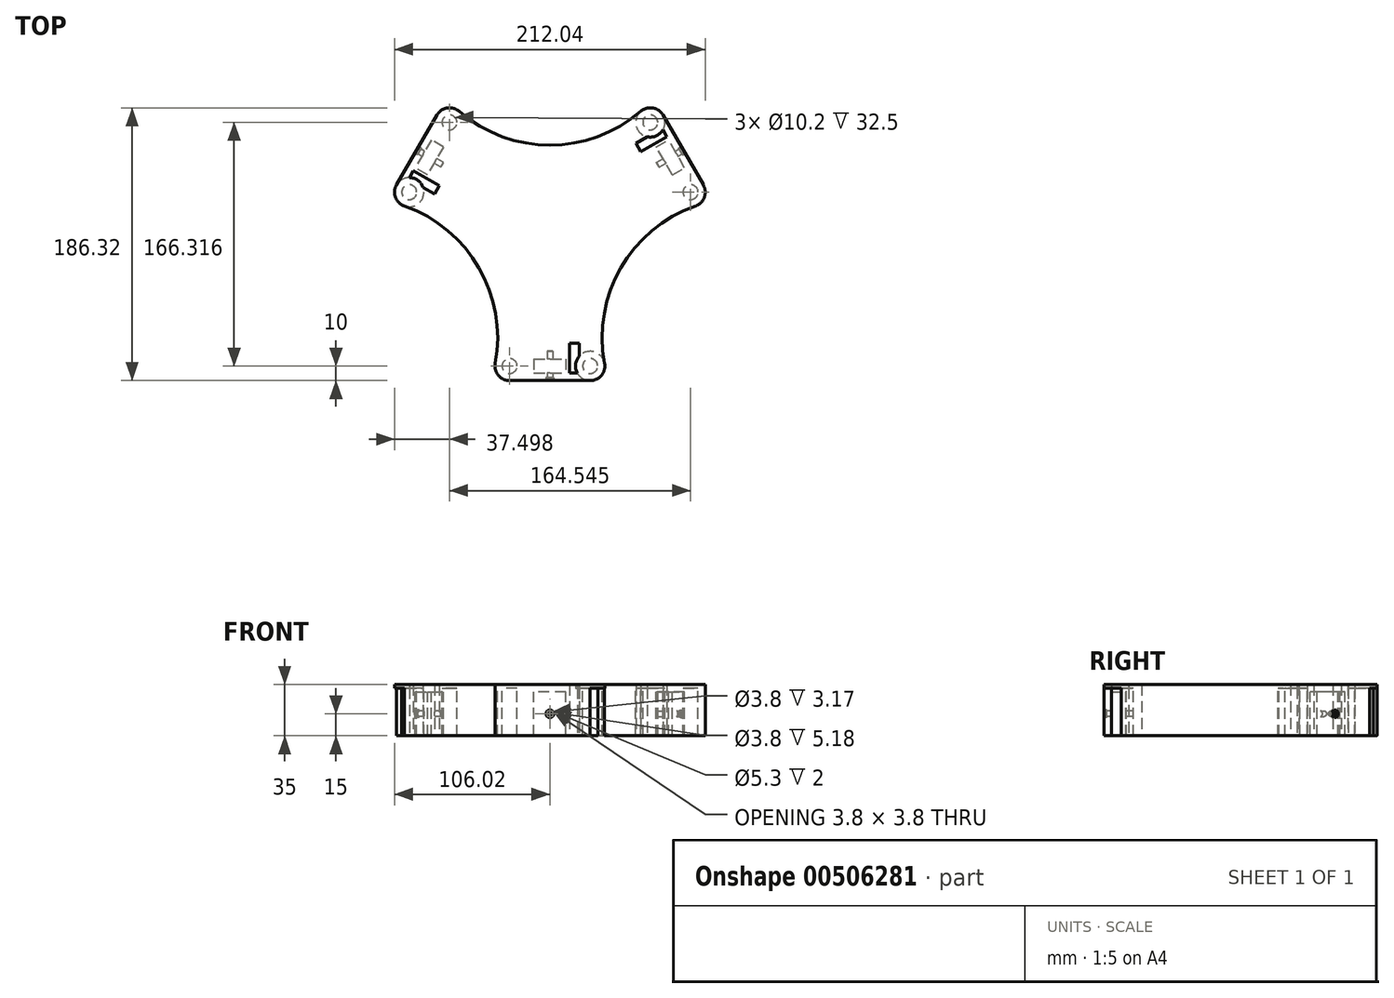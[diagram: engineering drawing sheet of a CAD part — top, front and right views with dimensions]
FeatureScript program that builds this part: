
annotation { "Feature Type Name" : "Feature", "Feature Type Description" : "" }
export const myFeature = defineFeature(function(context is Context, id is Id, definition is map)
    precondition{}
    {
        {
            var Q0;
            Q0=qCreatedBy(makeId("Top.planeOp"),FACE);
            var sketch = newSketch(context, id + "F0", { "sketchPlane" : qUnion([Q0])});
            skCircle(sketch, "E0", {"center": v(0, 0) * mm, "radius": 57.15 * mm, "construction": true});
            skLineSegment(sketch, "E1.bottom", {"start": v(110, -110) * mm, "end": v(-110, -110) * mm, "construction": true});
            skLineSegment(sketch, "E1.top", {"start": v(110, 110) * mm, "end": v(-110, 110) * mm, "construction": true});
            skLineSegment(sketch, "E1.left", {"start": v(110, -110) * mm, "end": v(110, 110) * mm, "construction": true});
            skLineSegment(sketch, "E1.right", {"start": v(-110, -110) * mm, "end": v(-110, 110) * mm, "construction": true});
            skLineSegment(sketch, "E2", {"start": v(0, 0) * mm, "end": v(0, -95) * mm});
            skLineSegment(sketch, "E3", {"start": v(0, 0) * mm, "end": v(-69.71, -40.25) * mm});
            skLineSegment(sketch, "E4", {"start": v(0, 0) * mm, "end": v(-77.38, 44.67) * mm});
            skLineSegment(sketch, "E5.MirrorCS", {"start": v(0, 0) * mm, "end": v(69.71, -40.25) * mm});
            skLineSegment(sketch, "E6.MirrorCS", {"start": v(0, 0) * mm, "end": v(77.38, 44.67) * mm});
            skCircle(sketch, "E7", {"center": v(-27.5, -95) * mm, "radius": 5.1 * mm});
            skCircle(sketch, "E8", {"center": v(-27.5, -95) * mm, "radius": 10 * mm});
            skCircle(sketch, "E9.MirrorC", {"center": v(27.5, -95) * mm, "radius": 5.1 * mm});
            skCircle(sketch, "E10.MirrorC", {"center": v(27.5, -95) * mm, "radius": 10 * mm});
            skLineSegment(sketch, "E11", {"start": v(-27.5, -105) * mm, "end": v(27.5, -105) * mm});
            skCircle(sketch, "E12.1.0", {"center": v(96.02, 23.68) * mm, "radius": 5.1 * mm});
            skCircle(sketch, "E12.1.1", {"center": v(96.02, 23.68) * mm, "radius": 10 * mm});
            skLineSegment(sketch, "E12.1.2", {"start": v(104.68, 28.68) * mm, "end": v(77.18, 76.32) * mm});
            skCircle(sketch, "E12.1.3", {"center": v(68.52, 71.32) * mm, "radius": 10 * mm});
            skCircle(sketch, "E12.1.4", {"center": v(68.52, 71.32) * mm, "radius": 5.1 * mm});
            skCircle(sketch, "E12.2.0", {"center": v(-68.52, 71.32) * mm, "radius": 5.1 * mm});
            skCircle(sketch, "E12.2.1", {"center": v(-68.52, 71.32) * mm, "radius": 10 * mm});
            skLineSegment(sketch, "E12.2.2", {"start": v(-77.18, 76.32) * mm, "end": v(-104.68, 28.68) * mm});
            skCircle(sketch, "E12.2.3", {"center": v(-96.02, 23.68) * mm, "radius": 10 * mm});
            skCircle(sketch, "E12.2.4", {"center": v(-96.02, 23.68) * mm, "radius": 5.1 * mm});
            skArc(sketch, "E13", {"start": v(99.32, 14.24) * mm, "mid": v(48.39, -27.94) * mm, "end": v(37.32, -93.14) * mm});
            skArc(sketch, "E14.1.0", {"start": v(-62, 78.9) * mm, "mid": v(0, 55.87) * mm, "end": v(62, 78.9) * mm});
            skArc(sketch, "E14.2.0", {"start": v(-37.32, -93.14) * mm, "mid": v(-48.39, -27.94) * mm, "end": v(-99.32, 14.24) * mm});
            skSolve(sketch);
        }
        {
            var Q0;
            {var subQ0=sQuery(id+"F0.wireOp",EDGE,"E11");Q0=makeQuery(id+"F0.imprint","IMPRINT",FACE,{"disambiguationData":[TD([[makeQuery(id+"F0.imprint","IMPRINT",EDGE,{"derivedFrom":subQ0}),1.0]])]});}
            var Q1;
            Q1=makeQuery(id+"F0.imprint","IMPRINT",FACE,{"disambiguationData":[TD([[makeQuery(id+"F0.imprint","IMPRINT",EDGE,{"derivedFrom":sQuery(id+"F0.wireOp",EDGE,"E9.MirrorC")}),1.0]])]});
            var Q2;
            Q2=makeQuery(id+"F0.imprint","IMPRINT",FACE,{"disambiguationData":[TD([[makeQuery(id+"F0.imprint","IMPRINT",EDGE,{"derivedFrom":sQuery(id+"F0.wireOp",EDGE,"E7")}),-1.0]])]});
            extrude(context, id + "F1", {"entities" : qUnion([Q0, Q1, Q2]), "oppositeDirection" : true, "depth" : 35 * mm});
        }
        {
            var Q0;
            {var subQ0=sQuery(id+"F0.wireOp",EDGE,"E11");Q0=makeQuery(id+"F0.imprint","IMPRINT",FACE,{"disambiguationData":[TD([[makeQuery(id+"F0.imprint","IMPRINT",EDGE,{"derivedFrom":subQ0}),1.0]])]});}
            var sketch = newSketch(context, id + "F2", { "sketchPlane" : qUnion([Q0])});
            skLineSegment(sketch, "E15.0", {"start": v(-27.5, -105) * mm, "end": v(27.5, -105) * mm});
            skLineSegment(sketch, "E16.bottom", {"start": v(11, -99.83) * mm, "end": v(-11, -99.83) * mm});
            skLineSegment(sketch, "E16.top", {"start": v(11, -90.18) * mm, "end": v(-11, -90.18) * mm});
            skLineSegment(sketch, "E16.left", {"start": v(11, -99.83) * mm, "end": v(11, -90.18) * mm});
            skLineSegment(sketch, "E16.right", {"start": v(-11, -99.83) * mm, "end": v(-11, -90.18) * mm});
            skPoint(sketch, "E16.middle", {"position": v(0, -95) * mm});
            skPoint(sketch, "E16.middle.positionSnap0", {"position": v(0, -105) * mm});
            skPoint(sketch, "E16.centerSnap0", {"position": v(0, -105) * mm});
            skSolve(sketch);
        }
        {
            var Q0;
            Q0=makeQuery(id+"F2.imprint","IMPRINT",FACE,{"disambiguationData":[TD([[makeQuery(id+"F2.imprint","IMPRINT",EDGE,{"derivedFrom":sQuery(id+"F2.wireOp",EDGE,"E16.bottom")}),-1.0]])]});
            var Q1;
            Q1=makeQuery(id+"F1.opExtrude","CAP_FACE",FACE,{"disambiguationData":[OSD([sQuery(id+"F0.wireOp",EDGE,"E3"),sQuery(id+"F0.wireOp",EDGE,"E5.MirrorCS"),sQuery(id+"F0.wireOp",EDGE,"E7"),sQuery(id+"F0.wireOp",EDGE,"E8"),sQuery(id+"F0.wireOp",EDGE,"E9.MirrorC"),sQuery(id+"F0.wireOp",EDGE,"E10.MirrorC"),sQuery(id+"F0.wireOp",EDGE,"E11"),sQuery(id+"F0.wireOp",EDGE,"E13"),sQuery(id+"F0.wireOp",EDGE,"E14.2.0")])],"isStart":false});
            extrude(context, id + "F3", {"entities" : qUnion([Q0]), "operationType" : NewBodyOperationType.REMOVE, "endBound" : BoundingType.UP_TO_SURFACE, "oppositeDirection" : true, "endBoundEntityFace" : qUnion([Q1]), "depth" : 25 * mm});
        }
        {
            var Q0;
            Q0=makeQuery(id+"F2.imprint","IMPRINT",FACE,{"disambiguationData":[TD([[makeQuery(id+"F2.imprint","IMPRINT",EDGE,{"derivedFrom":sQuery(id+"F2.wireOp",EDGE,"E16.bottom")}),-1.0]])]});
            extrude(context, id + "F4", {"entities" : qUnion([Q0]), "operationType" : NewBodyOperationType.ADD, "oppositeDirection" : true, "depth" : 5 * mm});
        }
        {
            var Q0;
            Q0=makeQuery(id+"F0.imprint","IMPRINT",FACE,{"disambiguationData":[TD([[makeQuery(id+"F0.imprint","IMPRINT",EDGE,{"derivedFrom":sQuery(id+"F0.wireOp",EDGE,"E7")}),1.0]])]});
            var Q1;
            Q1=makeQuery(id+"F0.imprint","IMPRINT",FACE,{"disambiguationData":[TD([[makeQuery(id+"F0.imprint","IMPRINT",EDGE,{"derivedFrom":sQuery(id+"F0.wireOp",EDGE,"E9.MirrorC")}),-1.0]])]});
            var Q2;
            Q2=sQuery(id+"F0.wireOp",EDGE,"E7");
            var Q3;
            Q3=sQuery(id+"F0.wireOp",EDGE,"E9.MirrorC");
            extrude(context, id + "F5", {"entities" : qUnion([Q0, Q1]), "operationType" : NewBodyOperationType.ADD, "surfaceEntities" : qUnion([Q2, Q3]), "oppositeDirection" : true, "depth" : 2.5 * mm});
        }
        {
            var Q0;
            Q0=makeQuery(id+"F1.opExtrude","SWEPT_FACE",FACE,{"disambiguationData":[OSD([sQuery(id+"F0.wireOp",EDGE,"E11")])]});
            var sketch = newSketch(context, id + "F6", { "sketchPlane" : qUnion([Q0])});
            skLineSegment(sketch, "E17.0", {"start": v(-27.5, -35) * mm, "end": v(27.5, -35) * mm});
            skLineSegment(sketch, "E18.0", {"start": v(-27.5, 0) * mm, "end": v(27.5, 0) * mm});
            skLineSegment(sketch, "E19", {"start": v(0, 0) * mm, "end": v(0, -35) * mm, "construction": true});
            skPoint(sketch, "E20", {"position": v(0, -17.5) * mm});
            skCircle(sketch, "E21", {"center": v(0, -20) * mm, "radius": 4.15 * mm});
            skCircle(sketch, "E22", {"center": v(0, -20) * mm, "radius": 2.65 * mm});
            skCircle(sketch, "E23", {"center": v(0, -20) * mm, "radius": 1.9 * mm});
            skSolve(sketch);
        }
        {
            var Q0;
            Q0=makeQuery(id+"F6.imprint","IMPRINT",FACE,{"disambiguationData":[TD([[makeQuery(id+"F6.imprint","IMPRINT",EDGE,{"derivedFrom":sQuery(id+"F6.wireOp",EDGE,"E23")}),1.0]])]});
            extrude(context, id + "F7", {"entities" : qUnion([Q0]), "operationType" : NewBodyOperationType.REMOVE, "oppositeDirection" : true, "depth" : 20 * mm});
        }
        {
            var Q0;
            Q0=makeQuery(id+"F6.imprint","IMPRINT",FACE,{"disambiguationData":[TD([[makeQuery(id+"F6.imprint","IMPRINT",EDGE,{"derivedFrom":sQuery(id+"F6.wireOp",EDGE,"E22")}),1.0]])]});
            extrude(context, id + "F8", {"entities" : qUnion([Q0]), "operationType" : NewBodyOperationType.REMOVE, "oppositeDirection" : true, "depth" : 2 * mm});
        }
        {
            var Q0;
            Q0=makeQuery(id+"F1.opExtrude","CAP_FACE",FACE,{"disambiguationData":[OSD([sQuery(id+"F0.wireOp",EDGE,"E3"),sQuery(id+"F0.wireOp",EDGE,"E5.MirrorCS"),sQuery(id+"F0.wireOp",EDGE,"E7"),sQuery(id+"F0.wireOp",EDGE,"E8"),sQuery(id+"F0.wireOp",EDGE,"E9.MirrorC"),sQuery(id+"F0.wireOp",EDGE,"E10.MirrorC"),sQuery(id+"F0.wireOp",EDGE,"E11"),sQuery(id+"F0.wireOp",EDGE,"E13"),sQuery(id+"F0.wireOp",EDGE,"E14.2.0")])],"isStart":false});
            var sketch = newSketch(context, id + "F9", { "sketchPlane" : qUnion([Q0])});
            skLineSegment(sketch, "E24.bottom", {"start": v(20.02, 79.43) * mm, "end": v(13.37, 79.43) * mm});
            skLineSegment(sketch, "E24.top", {"start": v(20.02, 99.83) * mm, "end": v(13.37, 99.83) * mm});
            skLineSegment(sketch, "E24.left", {"start": v(20.02, 79.43) * mm, "end": v(20.02, 99.83) * mm});
            skLineSegment(sketch, "E24.right", {"start": v(13.37, 79.43) * mm, "end": v(13.37, 99.83) * mm});
            skPoint(sketch, "E24.middle", {"position": v(16.7, 89.63) * mm});
            skLineSegment(sketch, "E25.0", {"start": v(11, 90.18) * mm, "end": v(11, 99.83) * mm});
            skCircle(sketch, "E26.0", {"center": v(27.5, 95) * mm, "radius": 5.1 * mm});
            skLineSegment(sketch, "E27", {"start": v(22.4, 95) * mm, "end": v(20.02, 95) * mm});
            skLineSegment(sketch, "E28.trimOffspring", {"start": v(13.37, 95) * mm, "end": v(11, 95) * mm});
            skSolve(sketch);
        }
        {
            var Q0;
            {var subQ3=sQuery(id+"F9.wireOp",EDGE,"E24.bottom");Q0=makeQuery(id+"F9.imprint","IMPRINT",FACE,{"disambiguationData":[TD([[makeQuery(id+"F9.imprint","IMPRINT",EDGE,{"derivedFrom":subQ3}),-1.0]])]});}
            var Q1;
            {var subQ0=sQuery(id+"F0.wireOp",EDGE,"E9.MirrorC");var subQ1=sQuery(id+"F0.wireOp",EDGE,"E7");Q1=makeQuery(id+"F5.boolean.opBoolean","MERGE",FACE,{"derivedFrom":[makeQuery(id+"F4.boolean.opBoolean","MERGE",FACE,{"derivedFrom":[makeQuery(id+"F1.opExtrude","CAP_FACE",FACE,{"disambiguationData":[OSD([sQuery(id+"F0.wireOp",EDGE,"E3"),sQuery(id+"F0.wireOp",EDGE,"E5.MirrorCS"),subQ1,sQuery(id+"F0.wireOp",EDGE,"E8"),subQ0,sQuery(id+"F0.wireOp",EDGE,"E10.MirrorC"),sQuery(id+"F0.wireOp",EDGE,"E11"),sQuery(id+"F0.wireOp",EDGE,"E13"),sQuery(id+"F0.wireOp",EDGE,"E14.2.0")])],"isStart":true}),makeQuery(id+"F4.opExtrude","CAP_FACE",FACE,{"disambiguationData":[OSD([sQuery(id+"F2.wireOp",EDGE,"E16.bottom"),sQuery(id+"F2.wireOp",EDGE,"E16.top"),sQuery(id+"F2.wireOp",EDGE,"E16.left"),sQuery(id+"F2.wireOp",EDGE,"E16.right")])],"isStart":true})]}),makeQuery(id+"F5.opExtrude","CAP_FACE",FACE,{"disambiguationData":[OSD([subQ1])],"isStart":true}),makeQuery(id+"F5.opExtrude","CAP_FACE",FACE,{"disambiguationData":[OSD([subQ0])],"isStart":true})]});}
            extrude(context, id + "F10", {"entities" : qUnion([Q0]), "operationType" : NewBodyOperationType.REMOVE, "endBound" : BoundingType.UP_TO_SURFACE, "oppositeDirection" : true, "endBoundEntityFace" : qUnion([Q1]), "depth" : 25 * mm});
        }
        {
            var Q0;
            Q0=makeQuery(id+"F1.opExtrude","SWEPT_BODY",BODY,{"disambiguationData":[OSD([sQuery(id+"F0.wireOp",EDGE,"E3"),sQuery(id+"F0.wireOp",EDGE,"E5.MirrorCS"),sQuery(id+"F0.wireOp",EDGE,"E7"),sQuery(id+"F0.wireOp",EDGE,"E8"),sQuery(id+"F0.wireOp",EDGE,"E9.MirrorC"),sQuery(id+"F0.wireOp",EDGE,"E10.MirrorC"),sQuery(id+"F0.wireOp",EDGE,"E11"),sQuery(id+"F0.wireOp",EDGE,"E13"),sQuery(id+"F0.wireOp",EDGE,"E14.2.0")])]});
            var Q1;
            Q1=sQuery(id+"F0.wireOp",EDGE,"E0");
            circularPattern(context, id + "F11", {"operationType" : NewBodyOperationType.ADD, "entities" : qUnion([Q0]), "axis" : qUnion([Q1]), "angle" : 240 * degree, "instanceCount" : 3, "equalSpace" : true});
        }
    });
